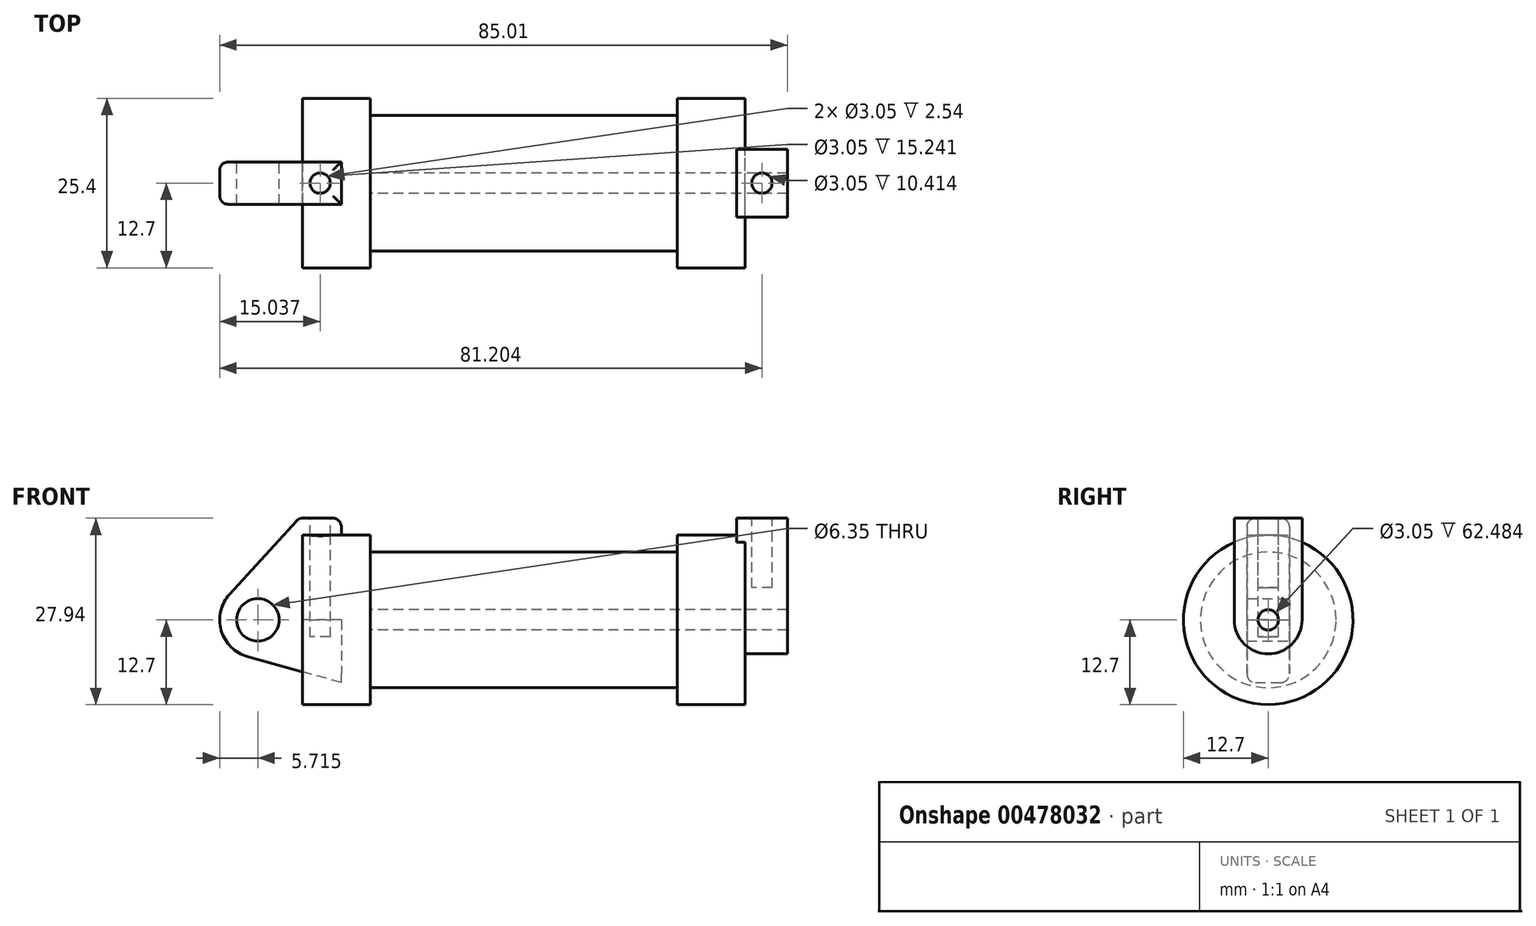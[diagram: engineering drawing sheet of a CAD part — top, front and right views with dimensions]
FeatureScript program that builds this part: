
annotation { "Feature Type Name" : "Feature", "Feature Type Description" : "" }
export const myFeature = defineFeature(function(context is Context, id is Id, definition is map)
    precondition{}
    {
        {
            var Q0;
            Q0=qCreatedBy(makeId("Front.planeOp"),FACE);
            var sketch = newSketch(context, id + "F0", { "sketchPlane" : qUnion([Q0])});
            skLineSegment(sketch, "E0", {"start": v(0, 0) * mm, "end": v(0, 12.7) * mm});
            skLineSegment(sketch, "E1", {"start": v(0, 12.7) * mm, "end": v(10.16, 12.7) * mm});
            skLineSegment(sketch, "E2", {"start": v(10.16, 12.7) * mm, "end": v(10.16, 10.16) * mm});
            skLineSegment(sketch, "E3", {"start": v(10.16, 10.16) * mm, "end": v(56.13, 10.16) * mm});
            skLineSegment(sketch, "E4", {"start": v(56.13, 10.16) * mm, "end": v(56.13, 12.7) * mm});
            skLineSegment(sketch, "E5", {"start": v(56.13, 12.7) * mm, "end": v(66.3, 12.7) * mm});
            skLineSegment(sketch, "E6", {"start": v(66.3, 12.7) * mm, "end": v(66.3, 0) * mm});
            skLineSegment(sketch, "E7", {"start": v(66.3, 0) * mm, "end": v(0, 0) * mm});
            skLineSegment(sketch, "E8", {"start": v(5.84, 15.24) * mm, "end": v(-0.5, 15.24) * mm});
            skLineSegment(sketch, "E9", {"start": v(-0.5, 15.24) * mm, "end": v(-10.88, 3.85) * mm});
            skLineSegment(sketch, "E10", {"start": v(0, 0) * mm, "end": v(-6.65, 0) * mm});
            skCircle(sketch, "E11", {"center": v(-6.65, 0) * mm, "radius": 5.72 * mm});
            skCircle(sketch, "E12", {"center": v(-6.65, 0) * mm, "radius": 3.18 * mm});
            skLineSegment(sketch, "E13", {"start": v(5.84, 15.24) * mm, "end": v(5.84, -9.4) * mm});
            skLineSegment(sketch, "E14", {"start": v(5.84, -9.4) * mm, "end": v(-8.18, -5.5) * mm});
            skSolve(sketch);
        }
        {
            var Q0;
            {var subQ0=sQuery(id+"F0.wireOp",EDGE,"E2");Q0=makeQuery(id+"F0.imprint","IMPRINT",FACE,{"disambiguationData":[TD([[makeQuery(id+"F0.imprint","IMPRINT",EDGE,{"derivedFrom":subQ0}),-1.0]])]});}
            var Q1;
            {var subQ0=sQuery(id+"F0.wireOp",EDGE,"E0");Q1=makeQuery(id+"F0.imprint","IMPRINT",FACE,{"disambiguationData":[TD([[makeQuery(id+"F0.imprint","IMPRINT",EDGE,{"derivedFrom":subQ0}),-1.0]])]});}
            var Q2;
            Q2=sQuery(id+"F0.wireOp",EDGE,"E10");
            revolve(context, id + "F1", {"entities" : qUnion([Q0, Q1]), "axis" : qUnion([Q2]), "revolveType" : RevolveType.FULL});
        }
        {
            var Q0;
            {var subQ5=sQuery(id+"F0.wireOp",EDGE,"E12");Q0=makeQuery(id+"F0.imprint","IMPRINT",FACE,{"disambiguationData":[TD([[makeQuery(id+"F0.imprint","IMPRINT",EDGE,{"derivedFrom":subQ5}),-1.0]])]});}
            var Q1;
            {var subQ1=sQuery(id+"F0.wireOp",EDGE,"E0");Q1=makeQuery(id+"F0.imprint","IMPRINT",FACE,{"disambiguationData":[TD([[makeQuery(id+"F0.imprint","IMPRINT",EDGE,{"derivedFrom":subQ1}),1.0]])]});}
            var Q2;
            {var subQ0=sQuery(id+"F0.wireOp",EDGE,"E14");Q2=makeQuery(id+"F0.imprint","IMPRINT",FACE,{"disambiguationData":[TD([[makeQuery(id+"F0.imprint","IMPRINT",EDGE,{"derivedFrom":subQ0}),-1.0]])]});}
            extrude(context, id + "F2", {"entities" : qUnion([Q0, Q1, Q2]), "endBound" : BoundingType.SYMMETRIC, "depth" : 6.35 * mm});
        }
        {
            var Q0;
            Q0=makeQuery(id+"F1.opRevolve","SWEPT_FACE",FACE,{"disambiguationData":[OSD([sQuery(id+"F0.wireOp",EDGE,"E6")])]});
            var sketch = newSketch(context, id + "F3", { "sketchPlane" : qUnion([Q0])});
            skCircle(sketch, "E15", {"center": v(0, 0) * mm, "radius": 1.52 * mm});
            skCircle(sketch, "E16", {"center": v(0, 0) * mm, "radius": 5.08 * mm});
            skLineSegment(sketch, "E17", {"start": v(-5.08, 0) * mm, "end": v(-5.08, 15.24) * mm});
            skLineSegment(sketch, "E18", {"start": v(5.08, 0) * mm, "end": v(5.08, 15.24) * mm});
            skLineSegment(sketch, "E19", {"start": v(-5.08, 15.24) * mm, "end": v(5.08, 15.24) * mm});
            skSolve(sketch);
        }
        {
            var Q0;
            {var subQ0=sQuery(id+"F3.wireOp",EDGE,"E19");Q0=makeQuery(id+"F3.imprint","IMPRINT",FACE,{"disambiguationData":[TD([[makeQuery(id+"F3.imprint","IMPRINT",EDGE,{"derivedFrom":subQ0}),-1.0]])]});}
            var Q1;
            {var subQ0=sQuery(id+"F3.wireOp",EDGE,"E17");var subQ1=sQuery(id+"F3.wireOp",EDGE,"E16");var subQ2=makeQuery(id+"F3.imprint","INTERSECT",VERTEX,{"derivedFrom":[subQ1,subQ0]});Q1=makeQuery(id+"F3.imprint","IMPRINT",FACE,{"disambiguationData":[TD([[makeQuery(id+"F3.imprint","IMPRINT",EDGE,{"disambiguationData":[TD([[subQ2,1.0]])],"derivedFrom":subQ1}),-1.0]])]});}
            var Q2;
            Q2=makeQuery(id+"F3.imprint","IMPRINT",FACE,{"disambiguationData":[TD([[makeQuery(id+"F3.imprint","IMPRINT",EDGE,{"derivedFrom":sQuery(id+"F3.wireOp",EDGE,"E15")}),-1.0]])]});
            extrude(context, id + "F4", {"entities" : qUnion([Q0, Q1, Q2]), "operationType" : NewBodyOperationType.ADD, "depth" : 6.35 * mm});
        }
        {
            var Q0;
            Q0=makeQuery(id+"F4.opExtrude","CAP_FACE",FACE,{"disambiguationData":[OSD([sQuery(id+"F3.wireOp",EDGE,"E15"),sQuery(id+"F3.wireOp",EDGE,"E16"),sQuery(id+"F3.wireOp",EDGE,"E17"),sQuery(id+"F3.wireOp",EDGE,"E18"),sQuery(id+"F3.wireOp",EDGE,"E19")])],"isStart":true});
            extrude(context, id + "F5", {"entities" : qUnion([Q0]), "operationType" : NewBodyOperationType.ADD, "depth" : 1.27 * mm});
        }
        {
            var Q0;
            Q0=makeQuery(id+"F4.boolean.opBoolean","SPLIT",FACE,{"disambiguationData":[TD([makeQuery(id+"F4.opExtrude","SWEPT_FACE",FACE,{"disambiguationData":[OSD([sQuery(id+"F3.wireOp",EDGE,"E15")])]})])],"derivedFrom":makeQuery(id+"F1.opRevolve","SWEPT_FACE",FACE,{"disambiguationData":[OSD([sQuery(id+"F0.wireOp",EDGE,"E6")])]})});
            var Q1;
            Q1=makeQuery(id+"F1.opRevolve","SWEPT_FACE",FACE,{"disambiguationData":[OSD([sQuery(id+"F0.wireOp",EDGE,"E2")])]});
            extrude(context, id + "F6", {"entities" : qUnion([Q0]), "operationType" : NewBodyOperationType.REMOVE, "endBound" : BoundingType.UP_TO_SURFACE, "oppositeDirection" : true, "endBoundEntityFace" : qUnion([Q1]), "depth" : 25.4 * mm});
        }
        {
            var Q0;
            Q0=makeQuery(id+"F2.opExtrude","SWEPT_FACE",FACE,{"disambiguationData":[OSD([sQuery(id+"F0.wireOp",EDGE,"E8")])]});
            var sketch = newSketch(context, id + "F7", { "sketchPlane" : qUnion([Q0])});
            skLineSegment(sketch, "E20.0", {"start": v(5.84, 3.18) * mm, "end": v(-0.5, 3.18) * mm});
            skPoint(sketch, "E21.0", {"position": v(2.67, -3.18) * mm});
            skLineSegment(sketch, "E22.0", {"start": v(-0.5, -3.18) * mm, "end": v(-0.5, 3.17) * mm});
            skLineSegment(sketch, "E23.0", {"start": v(5.84, -3.18) * mm, "end": v(5.84, 3.17) * mm});
            skCircle(sketch, "E24", {"center": v(2.67, 0) * mm, "radius": 1.52 * mm});
            skSolve(sketch);
        }
        {
            var Q0;
            Q0 = qSketchRegion(id + "F7", true);
            extrude(context, id + "F8", {"entities" : qUnion([Q0]), "operationType" : NewBodyOperationType.REMOVE, "oppositeDirection" : true, "depth" : 17.78 * mm});
        }
        {
            var Q0;
            {var subQ0=sQuery(id+"F3.wireOp",EDGE,"E19");Q0=makeQuery(id+"F5.boolean.opBoolean","MERGE",FACE,{"derivedFrom":[makeQuery(id+"F4.opExtrude","SWEPT_FACE",FACE,{"disambiguationData":[OSD([subQ0])]}),makeQuery(id+"F5.opExtrude","SWEPT_FACE",FACE,{"disambiguationData":[OSD([subQ0])]})]});}
            var sketch = newSketch(context, id + "F9", { "sketchPlane" : qUnion([Q0])});
            skCircle(sketch, "E25", {"center": v(68.83, 0) * mm, "radius": 1.52 * mm});
            skSolve(sketch);
        }
        {
            var Q0;
            Q0 = qSketchRegion(id + "F9", true);
            extrude(context, id + "F10", {"entities" : qUnion([Q0]), "operationType" : NewBodyOperationType.REMOVE, "oppositeDirection" : true, "depth" : 10.4 * mm});
        }
        {
            var Q0;
            Q0=makeQuery(id+"F1.opRevolve","SWEPT_EDGE",EDGE,{"disambiguationData":[OSD([sQuery(id+"F0.wireOp",EDGE,"E1"),sQuery(id+"F0.wireOp",EDGE,"E2")])]});
            var Q1;
            Q1=makeQuery(id+"F2.opExtrude","SWEPT_EDGE",EDGE,{"disambiguationData":[OSD([sQuery(id+"F0.wireOp",EDGE,"E8"),sQuery(id+"F0.wireOp",EDGE,"E13")])]});
            var Q2;
            Q2=makeQuery(id+"F2.opExtrude","CAP_EDGE",EDGE,{"disambiguationData":[OSD([sQuery(id+"F0.wireOp",EDGE,"E8")])],"isStart":false});
            var Q3;
            Q3=makeQuery(id+"F2.opExtrude","CAP_EDGE",EDGE,{"disambiguationData":[OSD([sQuery(id+"F0.wireOp",EDGE,"E8")])],"isStart":true});
            var Q4;
            Q4=makeQuery(id+"F2.opExtrude","SWEPT_EDGE",EDGE,{"disambiguationData":[OSD([sQuery(id+"F0.wireOp",EDGE,"E8"),sQuery(id+"F0.wireOp",EDGE,"E9")])]});
            var Q5;
            Q5=makeQuery(id+"F2.opExtrude","CAP_EDGE",EDGE,{"disambiguationData":[OSD([sQuery(id+"F0.wireOp",EDGE,"E9")])],"isStart":false});
            var Q6;
            Q6=makeQuery(id+"F2.opExtrude","CAP_EDGE",EDGE,{"disambiguationData":[OSD([sQuery(id+"F0.wireOp",EDGE,"E9")])],"isStart":true});
            var Q7;
            Q7=makeQuery(id+"F1.opRevolve","SWEPT_EDGE",EDGE,{"disambiguationData":[OSD([sQuery(id+"F0.wireOp",EDGE,"E0"),sQuery(id+"F0.wireOp",EDGE,"E1")])]});
            var Q8;
            Q8=makeQuery(id+"F1.opRevolve","SWEPT_EDGE",EDGE,{"disambiguationData":[OSD([sQuery(id+"F0.wireOp",EDGE,"E4"),sQuery(id+"F0.wireOp",EDGE,"E5")])]});
            var Q9;
            Q9=makeQuery(id+"F5.opExtrude","CAP_EDGE",EDGE,{"disambiguationData":[OSD([sQuery(id+"F3.wireOp",EDGE,"E19")])],"isStart":false});
            var Q10;
            {var subQ0=sQuery(id+"F3.wireOp",EDGE,"E19");var subQ1=sQuery(id+"F3.wireOp",EDGE,"E17");Q10=makeQuery(id+"F5.boolean.opBoolean","MERGE",EDGE,{"derivedFrom":[makeQuery(id+"F4.opExtrude","SWEPT_EDGE",EDGE,{"disambiguationData":[OSD([subQ1,subQ0])]}),makeQuery(id+"F5.opExtrude","SWEPT_EDGE",EDGE,{"disambiguationData":[OSD([subQ1,subQ0])]})]});}
            var Q11;
            Q11=makeQuery(id+"F4.opExtrude","CAP_EDGE",EDGE,{"disambiguationData":[OSD([sQuery(id+"F3.wireOp",EDGE,"E19")])],"isStart":false});
            var Q12;
            {var subQ0=sQuery(id+"F3.wireOp",EDGE,"E19");var subQ1=sQuery(id+"F3.wireOp",EDGE,"E18");Q12=makeQuery(id+"F5.boolean.opBoolean","MERGE",EDGE,{"derivedFrom":[makeQuery(id+"F4.opExtrude","SWEPT_EDGE",EDGE,{"disambiguationData":[OSD([subQ1,subQ0])]}),makeQuery(id+"F5.opExtrude","SWEPT_EDGE",EDGE,{"disambiguationData":[OSD([subQ1,subQ0])]})]});}
            var Q13;
            Q13=makeQuery(id+"F4.opExtrude","CAP_EDGE",EDGE,{"disambiguationData":[OSD([sQuery(id+"F3.wireOp",EDGE,"E18")])],"isStart":false});
            var Q14;
            {var subQ0=sQuery(id+"F0.wireOp",EDGE,"E5");var subQ1=sQuery(id+"F0.wireOp",EDGE,"E6");Q14=makeQuery(id+"F4.boolean.opBoolean","SPLIT",EDGE,{"disambiguationData":[topologyDisambiguationEdgeConnected([makeQuery(id+"F1.opRevolve","SWEPT_FACE",FACE,{"disambiguationData":[OSD([subQ1])]})])],"derivedFrom":makeQuery(id+"F1.opRevolve","SWEPT_EDGE",EDGE,{"disambiguationData":[OSD([subQ0,subQ1])]})});}
            var Q15;
            {var subQ0=sQuery(id+"F3.wireOp",EDGE,"E17");Q15=makeQuery(id+"F4.boolean.opBoolean","SPLIT",EDGE,{"disambiguationData":[topologyDisambiguationEdgeConnected([makeQuery(id+"F1.opRevolve","SWEPT_FACE",FACE,{"disambiguationData":[OSD([sQuery(id+"F0.wireOp",EDGE,"E6")])]})])],"derivedFrom":makeQuery(id+"F4.opExtrude","CAP_EDGE",EDGE,{"disambiguationData":[OSD([subQ0])],"isStart":true})});}
            fillet(context, id + "F11", {"entities" : qUnion([Q0, Q1, Q2, Q3, Q4, Q5, Q6, Q7, Q8, Q9, Q10, Q11, Q12, Q13, Q14, Q15]), "radius" : 1.27 * mm, "tangentPropagation" : true, "allowEdgeOverflow" : false});
        }
    });
